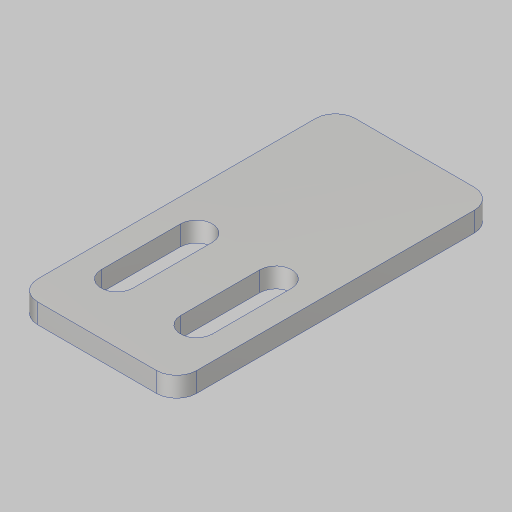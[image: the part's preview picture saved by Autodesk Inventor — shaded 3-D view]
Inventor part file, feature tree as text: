
AUTODESK INVENTOR PART (.ipt)
format: ipt  version: 2023.5 (Build 275446000, 446)  size: 202,752 bytes
history: native  units: in
note: dims shown in document units (in); Inventor stores cm internally (conversion verified against a paired STEP export)
features: sketch x5, extrude x5, fillet x4, projected_geometry x4
ambient origin geometry x8: Origin, YZ Plane, XZ Plane, XY Plane, X Axis, Y Axis, Z Axis, Center Point
bodies: Solid1 (feature_tree)
feature tree (18):
  sketch  "Sketch1"  dims[d1=0.7in d3=0.125in d4=0.197in]
  extrude  "Extrusion1"  Depth=0.125in
  fillet  "Fillet1"  Radius=0.197in
  extrude  "Extrusion2"  Depth=1.0in
  extrude  "Extrusion3"  Depth=0.5in
  fillet  "Fillet2"  Radius=0.5in
  extrude  "Extrusion4"  Depth=0.125in TaperAngle=0.0deg
  fillet  "Fillet3"  Radius=0.125in
  extrude  "Extrusion5"  Depth=0.5in
  fillet  "Fillet4"  Radius=1.375in
  sketch  "Sketch2"  dims[d5=0.197in d8=1.0in]
  sketch  "Sketch3"  dims[d9=2.0in d10=0.25in d11=0.5in]
  sketch  "Sketch4"  dims[d12=0.25in d13=0.125in d14=0.0in d22=0.125in]
  sketch  "Sketch5"  dims[d23=0.201in d24=0.5in d26=1.375in d27=0.5in d28=1.0in d29=0.0in d30=1.26in d31=0.5in d32=0.125in d33=1.0in d34=0.0in d35=0.125in d36=0.093in d37=0.042in d38=1.0in d39=0.0in d40=0.125in d41=0.7874in d43=0.197in d44=0.3937in d46=1.0in d48=1.8in d49=3.45in d50=1.125in d51=1.0in d52=0.0in d53=0.125in]
  projected_geometry  "Project Cut Edges1"
  projected_geometry  "Project Cut Edges2"
  projected_geometry  "Project Cut Edges3"
  projected_geometry  "Project Cut Edges4"
